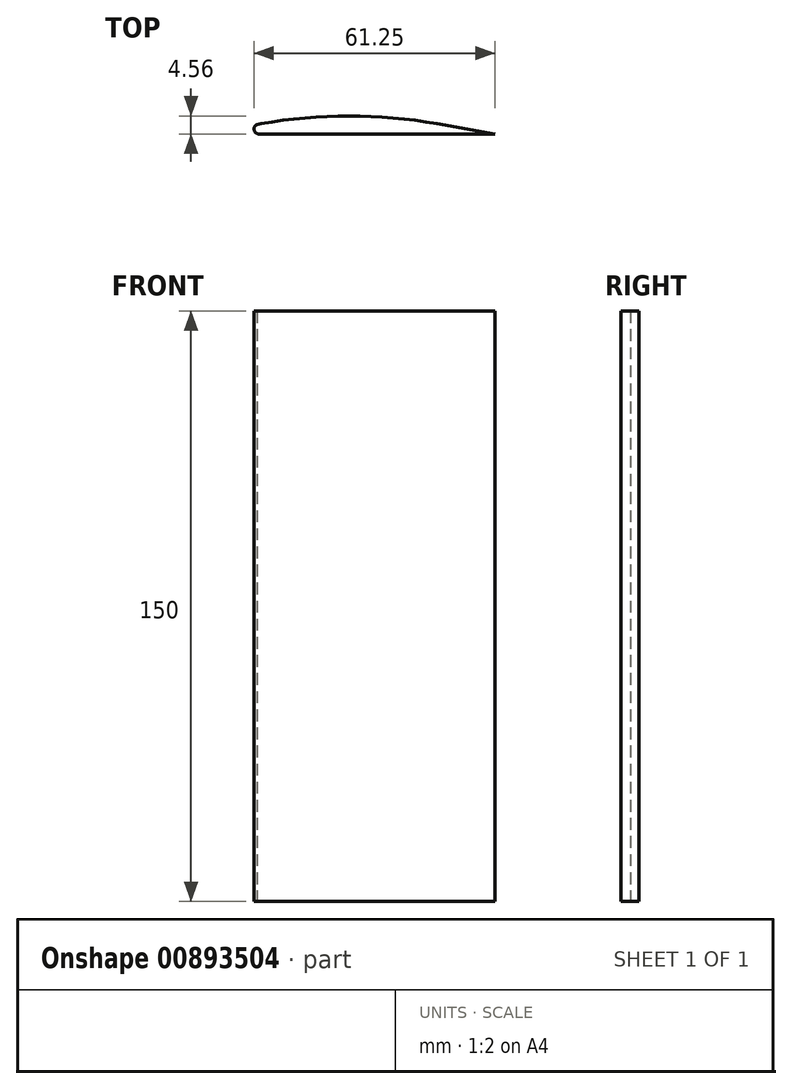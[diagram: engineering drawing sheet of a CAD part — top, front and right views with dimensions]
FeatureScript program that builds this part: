
annotation { "Feature Type Name" : "Feature", "Feature Type Description" : "" }
export const myFeature = defineFeature(function(context is Context, id is Id, definition is map)
    precondition{}
    {
        {
            var Q0;
            Q0=qCreatedBy(makeId("Top.planeOp"),FACE);
            var sketch = newSketch(context, id + "F0", { "sketchPlane" : qUnion([Q0])});
            skLineSegment(sketch, "E0", {"start": v(0, 0) * mm, "end": v(60, 0) * mm});
            skLineSegment(sketch, "E1", {"start": v(60, 0) * mm, "end": v(45.23, 2.6) * mm});
            skArc(sketch, "E2", {"start": v(45.23, 2.6) * mm, "mid": v(22.9, 4.56) * mm, "end": v(0.56, 2.6) * mm});
            skLineSegment(sketch, "E3", {"start": v(0, 0) * mm, "end": v(0, 6.84) * mm, "construction": true});
            skLineSegment(sketch, "E4", {"start": v(0.56, 2.6) * mm, "end": v(-0.43, 2.43) * mm});
            skLineSegment(sketch, "E5", {"start": v(0, 0) * mm, "end": v(-0.43, 2.43) * mm, "construction": true});
            skArc(sketch, "E6", {"start": v(0, 0) * mm, "mid": v(-1.23, 1.04) * mm, "end": v(-0.43, 2.43) * mm});
            skSolve(sketch);
        }
        {
            var Q0;
            Q0=makeQuery(id+"F0.imprint","IMPRINT",FACE,{"disambiguationData":[TD([[makeQuery(id+"F0.imprint","IMPRINT",EDGE,{"derivedFrom":sQuery(id+"F0.wireOp",EDGE,"E0")}),1.0]])]});
            extrude(context, id + "F1", {"entities" : qUnion([Q0]), "depth" : 150 * mm, "offsetDistance" : 25 * mm});
        }
    });
